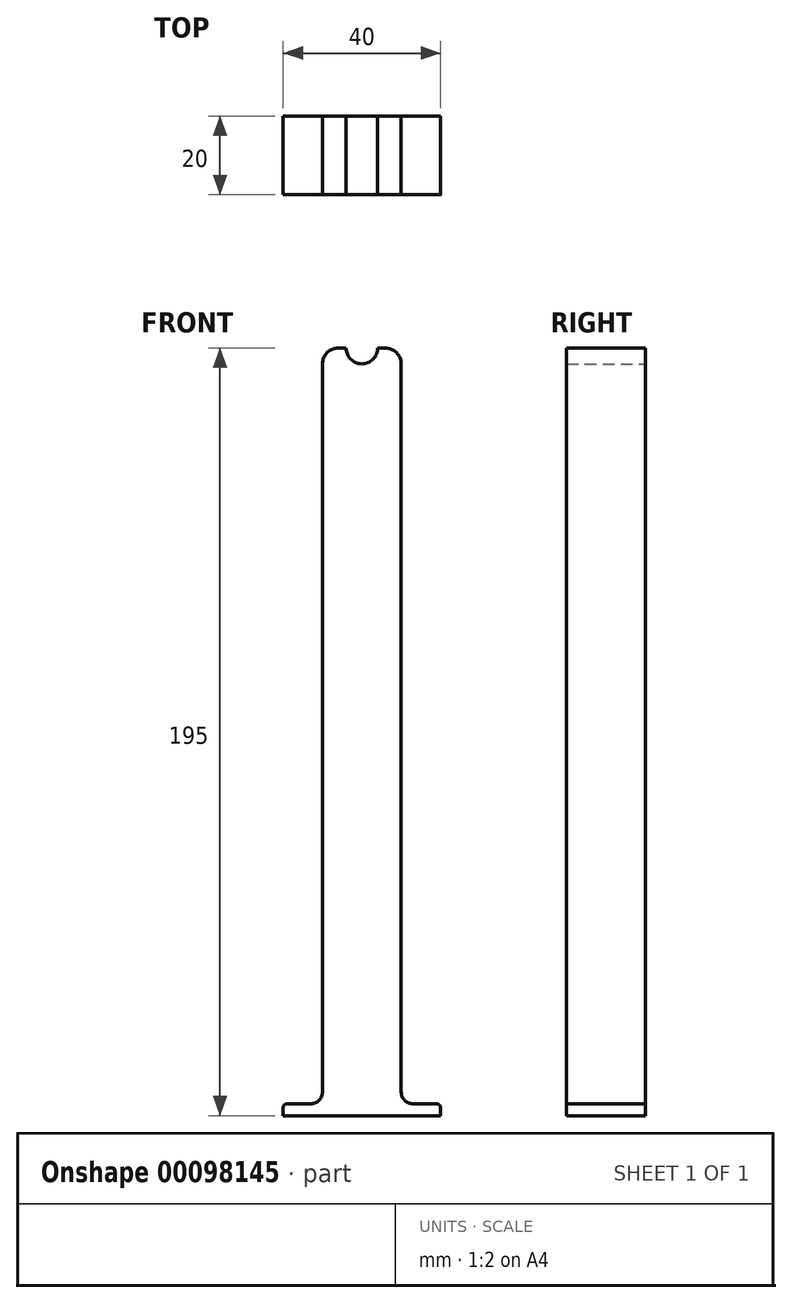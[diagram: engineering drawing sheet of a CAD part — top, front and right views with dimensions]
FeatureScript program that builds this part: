
annotation { "Feature Type Name" : "Feature", "Feature Type Description" : "" }
export const myFeature = defineFeature(function(context is Context, id is Id, definition is map)
    precondition{}
    {
        {
            var Q0;
            Q0=qCreatedBy(makeId("Front.planeOp"),FACE);
            var sketch = newSketch(context, id + "F0", { "sketchPlane" : qUnion([Q0])});
            skLineSegment(sketch, "E0", {"start": v(0, 0) * mm, "end": v(-20, 0) * mm});
            skLineSegment(sketch, "E1", {"start": v(-20, 0) * mm, "end": v(-20, 2) * mm});
            skLineSegment(sketch, "E2", {"start": v(-19, 3) * mm, "end": v(-13, 3) * mm});
            skPoint(sketch, "E2.endSnap0", {"position": v(-10, 0) * mm});
            skLineSegment(sketch, "E3", {"start": v(-10, 6) * mm, "end": v(-10, 191) * mm});
            skLineSegment(sketch, "E4", {"start": v(-6, 195) * mm, "end": v(0, 195) * mm});
            skLineSegment(sketch, "E5", {"start": v(0, 195) * mm, "end": v(0, 0) * mm});
            skPoint(sketch, "E6.visualSharp", {"position": v(-10, 195) * mm});
            skArc(sketch, "E6.filletArc", {"start": v(-6, 195) * mm, "mid": v(-8.83, 193.83) * mm, "end": v(-10, 191) * mm});
            skPoint(sketch, "E7.visualSharp", {"position": v(-10, 3) * mm});
            skArc(sketch, "E7.filletArc", {"start": v(-13, 3) * mm, "mid": v(-10.88, 3.88) * mm, "end": v(-10, 6) * mm});
            skPoint(sketch, "E8.visualSharp", {"position": v(-20, 3) * mm});
            skArc(sketch, "E8.filletArc", {"start": v(-19, 3) * mm, "mid": v(-19.7, 2.7) * mm, "end": v(-20, 2) * mm});
            skCircle(sketch, "E9", {"center": v(0, 195) * mm, "radius": 4 * mm});
            skSolve(sketch);
        }
        {
            var Q0;
            {var subQ1=sQuery(id+"F0.wireOp",EDGE,"E0");Q0=makeQuery(id+"F0.imprint","IMPRINT",FACE,{"disambiguationData":[TD([[makeQuery(id+"F0.imprint","IMPRINT",EDGE,{"derivedFrom":subQ1}),-1.0]])]});}
            extrude(context, id + "F1", {"entities" : qUnion([Q0]), "depth" : 20 * mm});
        }
        {
            var Q0;
            Q0=makeQuery(id+"F1.opExtrude","SWEPT_BODY",BODY,{"disambiguationData":[OSD([sQuery(id+"F0.wireOp",EDGE,"E0"),sQuery(id+"F0.wireOp",EDGE,"E1"),sQuery(id+"F0.wireOp",EDGE,"E2"),sQuery(id+"F0.wireOp",EDGE,"E3"),sQuery(id+"F0.wireOp",EDGE,"E4"),sQuery(id+"F0.wireOp",EDGE,"E5"),sQuery(id+"F0.wireOp",EDGE,"E6.filletArc"),sQuery(id+"F0.wireOp",EDGE,"E7.filletArc"),sQuery(id+"F0.wireOp",EDGE,"E8.filletArc"),sQuery(id+"F0.wireOp",EDGE,"E9")])]});
            var Q1;
            Q1=makeQuery(id+"F1.opExtrude","SWEPT_FACE",FACE,{"disambiguationData":[OSD([sQuery(id+"F0.wireOp",EDGE,"E5")])]});
            mirror(context, id + "F2", {"operationType" : NewBodyOperationType.ADD, "entities" : qUnion([Q0]), "mirrorPlane" : qUnion([Q1])});
        }
    });
